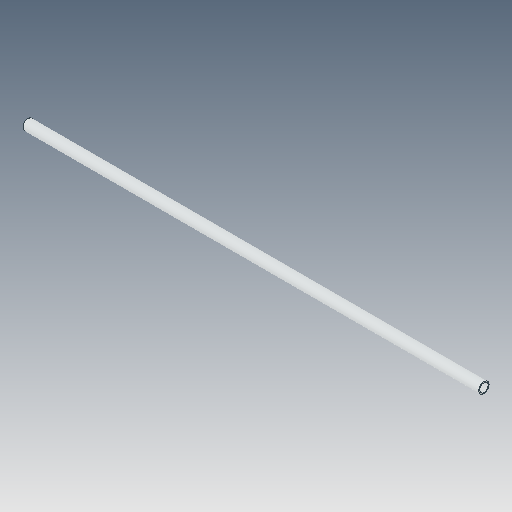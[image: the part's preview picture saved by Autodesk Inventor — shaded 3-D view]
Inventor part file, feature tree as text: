
AUTODESK INVENTOR PART (.ipt)
format: ipt  version: 2023.5 (Build 275446000, 446)  size: 93,696 bytes
history: native  units: in
note: dims shown in document units (in); Inventor stores cm internally (conversion verified against a paired STEP export)
features: mirror x1
ambient origin geometry x8: Origin, YZ Plane, XZ Plane, XY Plane, X Axis, Y Axis, Z Axis, Center Point
bodies: Solid1 (feature_tree)
feature tree (1):
  mirror  "Mirror1"
